# Revit family: JT8-24
name_source: partatom
category: Lighting Fixtures
revit_build: Autodesk Revit Architecture 2012 (Build: 20110309_2315(x64)
units: mm (PartAtom-declared; Revit-internal decimal feet)

## types (3) — shared parameters
Apparent Load = 0 VA
Color Filter = 16777215
Default Elevation = 48"
Description = Dedicated T8 Lensed Troffer
Dimming Lamp Color Temperature Shift = <None>
Emit from Line Length = 24"
Finish = Steel
Glass = Glass
Lamp = Four
Manufacturer = Columbia Lighting
Manufacturer Fax = (864)-678-1065
Model = JT8 24
Product Page URL = http://www.columbialighting.com
Product Specification Sheet = http://www.columbialighting.com
Tilt Angle = 90.00°
URL = http://www.columbialighting.com
Wattage Comments = 28-51 W

## per-type parameters (varying)
| type | Photometric Web File |
| JT824-232G-FSA12 | 13121.IES |
| JT824-332G-FSA12 | 13120.IES |
| JT824-432G-FSA12 | I52515.IES |

## geometry (parser evidence)
native form markers: Blend x1, Sweep x1
no freeform markers — native parametric forms only
